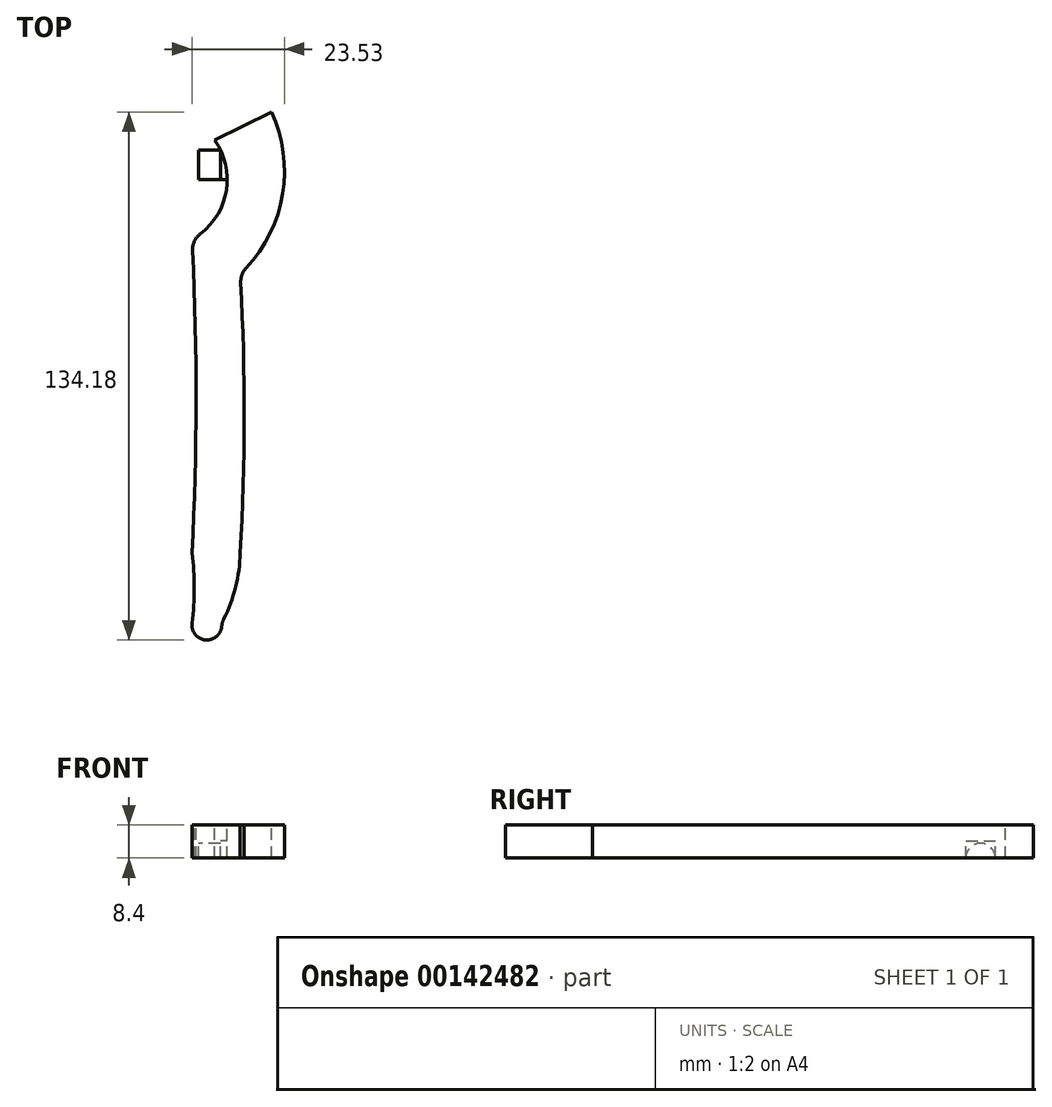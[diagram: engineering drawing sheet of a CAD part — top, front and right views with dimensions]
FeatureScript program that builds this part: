
annotation { "Feature Type Name" : "Feature", "Feature Type Description" : "" }
export const myFeature = defineFeature(function(context is Context, id is Id, definition is map)
    precondition{}
    {
        {
            var Q0;
            Q0=qCreatedBy(makeId("Top.planeOp"),FACE);
            var sketch = newSketch(context, id + "F0", { "sketchPlane" : qUnion([Q0])});
            skArc(sketch, "E0", {"start": v(-18.84, -33.1) * mm, "mid": v(-9.92, -17.2) * mm, "end": v(-18.84, -1.3) * mm});
            skArc(sketch, "E1", {"start": v(-9.22, -40.6) * mm, "mid": v(1.28, -22.3) * mm, "end": v(-0.84, -1.3) * mm});
            skArc(sketch, "E2", {"start": v(-18.84, -111.7) * mm, "mid": v(-17.84, -72.4) * mm, "end": v(-18.84, -33.1) * mm});
            skArc(sketch, "E3", {"start": v(-9.22, -112.4) * mm, "mid": v(-8.2, -76.5) * mm, "end": v(-9.22, -40.6) * mm});
            skArc(sketch, "E4", {"start": v(-18.84, -111.7) * mm, "mid": v(-14.2, -114.48) * mm, "end": v(-9.22, -112.4) * mm});
            skLineSegment(sketch, "E5", {"start": v(-0.84, -1.3) * mm, "end": v(-18.84, -1.3) * mm});
            skArc(sketch, "E6.0", {"start": v(-20.16, -112.1) * mm, "mid": v(-19.14, -72.24) * mm, "end": v(-20.18, -32.37) * mm});
            skLineSegment(sketch, "E6.1", {"start": v(0, 0) * mm, "end": v(-26.43, 0) * mm});
            skArc(sketch, "E6.2", {"start": v(-7.89, -41.14) * mm, "mid": v(2.7, -21.84) * mm, "end": v(0, 0) * mm});
            skArc(sketch, "E6.3", {"start": v(-20.18, -32.37) * mm, "mid": v(-11.53, -13.92) * mm, "end": v(-26.43, 0) * mm});
            skArc(sketch, "E6.4", {"start": v(-7.9, -112.1) * mm, "mid": v(-6.9, -76.62) * mm, "end": v(-7.89, -41.14) * mm});
            skArc(sketch, "E7", {"start": v(-20.16, -129.9) * mm, "mid": v(-19.6, -121) * mm, "end": v(-20.16, -112.1) * mm});
            skArc(sketch, "E8", {"start": v(-12.62, -129.9) * mm, "mid": v(-9.22, -121.28) * mm, "end": v(-7.9, -112.1) * mm});
            skArc(sketch, "E9", {"start": v(-20.16, -129.9) * mm, "mid": v(-16.4, -134.18) * mm, "end": v(-12.62, -129.9) * mm});
            skArc(sketch, "E10", {"start": v(-19.77, -125.92) * mm, "mid": v(-23.95, -127.51) * mm, "end": v(-20.16, -129.9) * mm});
            skCircle(sketch, "E11", {"center": v(-21.46, -127.76) * mm, "radius": 1 * mm});
            skLineSegment(sketch, "E12", {"start": v(-11.22, -17.2) * mm, "end": v(-18.52, -17.2) * mm});
            skLineSegment(sketch, "E13", {"start": v(-18.52, -17.2) * mm, "end": v(-18.52, -9.7) * mm});
            skLineSegment(sketch, "E14", {"start": v(-18.52, -9.7) * mm, "end": v(-12.93, -9.7) * mm});
            skLineSegment(sketch, "E15", {"start": v(0, 0) * mm, "end": v(-14.4, -7.2) * mm});
            skSolve(sketch);
        }
        {
            var Q0;
            {var subQ1=sQuery(id+"F0.wireOp",EDGE,"E1");Q0=makeQuery(id+"F0.imprint","IMPRINT",FACE,{"disambiguationData":[TD([[makeQuery(id+"F0.imprint","IMPRINT",EDGE,{"derivedFrom":subQ1}),1.0]])]});}
            var Q1;
            {var subQ8=sQuery(id+"F0.wireOp",EDGE,"E1");Q1=makeQuery(id+"F0.imprint","IMPRINT",FACE,{"disambiguationData":[TD([[makeQuery(id+"F0.imprint","IMPRINT",EDGE,{"derivedFrom":subQ8}),-1.0]])]});}
            extrude(context, id + "F1", {"entities" : qUnion([Q0, Q1]), "oppositeDirection" : true, "depth" : 8.4 * mm});
        }
        {
            var Q0;
            {var subQ0=sQuery(id+"F0.wireOp",EDGE,"E12");Q0=makeQuery(id+"F0.imprint","IMPRINT",FACE,{"disambiguationData":[TD([[makeQuery(id+"F0.imprint","IMPRINT",EDGE,{"derivedFrom":subQ0}),-1.0]])]});}
            extrude(context, id + "F2", {"entities" : qUnion([Q0]), "operationType" : NewBodyOperationType.ADD, "oppositeDirection" : true, "depth" : 8.4 * mm});
        }
        {
            var Q0;
            {var subQ0=sQuery(id+"F0.wireOp",EDGE,"E12");Q0=makeQuery(id+"F0.imprint","IMPRINT",FACE,{"disambiguationData":[TD([[makeQuery(id+"F0.imprint","IMPRINT",EDGE,{"derivedFrom":subQ0}),-1.0]])]});}
            extrude(context, id + "F3", {"entities" : qUnion([Q0]), "operationType" : NewBodyOperationType.REMOVE, "oppositeDirection" : true, "depth" : 4 * mm});
        }
        {
            var Q0;
            Q0=makeQuery(id+"F2.opExtrude","SWEPT_FACE",FACE,{"disambiguationData":[OSD([sQuery(id+"F0.wireOp",EDGE,"E13")])]});
            var sketch = newSketch(context, id + "F4", { "sketchPlane" : qUnion([Q0])});
            skLineSegment(sketch, "E16.0", {"start": v(17.2, -8.4) * mm, "end": v(9.7, -8.4) * mm});
            skLineSegment(sketch, "E16.1", {"start": v(17.2, -8.4) * mm, "end": v(17.2, -4) * mm});
            skLineSegment(sketch, "E16.2", {"start": v(17.2, -4) * mm, "end": v(9.7, -4) * mm});
            skLineSegment(sketch, "E16.3", {"start": v(9.7, -8.4) * mm, "end": v(9.7, -4) * mm});
            skArc(sketch, "E17", {"start": v(17.2, -8.4) * mm, "mid": v(13.45, -4.65) * mm, "end": v(9.7, -8.4) * mm});
            skSolve(sketch);
        }
        {
            var Q0;
            Q0=makeQuery(id+"F4.imprint","IMPRINT",FACE,{"disambiguationData":[TD([[makeQuery(id+"F4.imprint","IMPRINT",EDGE,{"derivedFrom":sQuery(id+"F4.wireOp",EDGE,"E16.1")}),1.0]])]});
            extrude(context, id + "F5", {"entities" : qUnion([Q0]), "operationType" : NewBodyOperationType.REMOVE, "oppositeDirection" : true, "depth" : 5.6 * mm});
        }
        {
            var Q0;
            Q0=makeQuery(id+"F1.opExtrude","SWEPT_EDGE",EDGE,{"disambiguationData":[OSD([sQuery(id+"F0.wireOp",EDGE,"E6.2"),sQuery(id+"F0.wireOp",EDGE,"E6.4")])]});
            var Q1;
            Q1=makeQuery(id+"F1.opExtrude","SWEPT_EDGE",EDGE,{"disambiguationData":[OSD([sQuery(id+"F0.wireOp",EDGE,"E6.0"),sQuery(id+"F0.wireOp",EDGE,"E6.3")])]});
            var Q2;
            Q2=makeQuery(id+"F1.opExtrude","SWEPT_EDGE",EDGE,{"disambiguationData":[OSD([sQuery(id+"F0.wireOp",EDGE,"E8"),sQuery(id+"F0.wireOp",EDGE,"E9")])]});
            fillet(context, id + "F6", {"entities" : qUnion([Q0, Q1, Q2]), "radius" : 5 * mm, "tangentPropagation" : true, "allowEdgeOverflow" : false});
        }
    });
